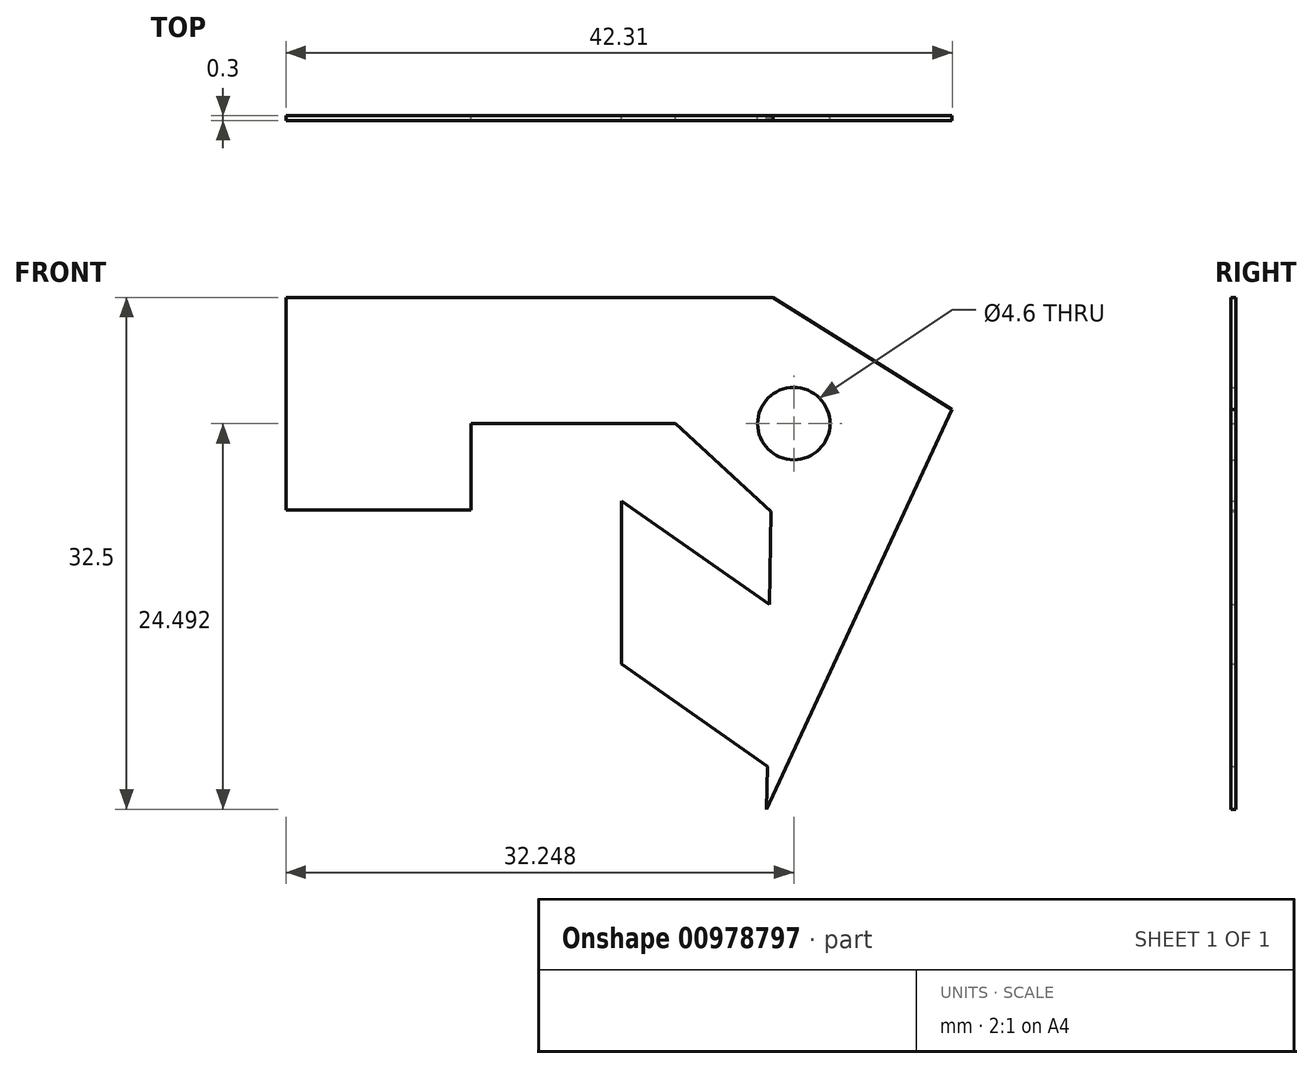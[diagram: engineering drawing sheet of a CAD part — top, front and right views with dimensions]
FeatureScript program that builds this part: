
annotation { "Feature Type Name" : "Feature", "Feature Type Description" : "" }
export const myFeature = defineFeature(function(context is Context, id is Id, definition is map)
    precondition{}
    {
        {
            var Q0;
            Q0=qCreatedBy(makeId("Front.planeOp"),FACE);
            var sketch = newSketch(context, id + "F0", { "sketchPlane" : qUnion([Q0])});
            skLineSegment(sketch, "E0", {"start": v(-25.77, 44.55) * mm, "end": v(5.15, 44.55) * mm});
            skLineSegment(sketch, "E1", {"start": v(5.15, 44.55) * mm, "end": v(16.54, 37.45) * mm});
            skLineSegment(sketch, "E2", {"start": v(16.54, 37.45) * mm, "end": v(4.75, 12.05) * mm});
            skLineSegment(sketch, "E3", {"start": v(16.54, 37.45) * mm, "end": v(16.54, 12.05) * mm, "construction": true});
            skLineSegment(sketch, "E4", {"start": v(4.75, 12.05) * mm, "end": v(16.54, 12.05) * mm, "construction": true});
            skLineSegment(sketch, "E5", {"start": v(-25.77, 44.55) * mm, "end": v(-25.77, 31.05) * mm});
            skLineSegment(sketch, "E6", {"start": v(-25.77, 31.05) * mm, "end": v(-14.03, 31.05) * mm});
            skLineSegment(sketch, "E7", {"start": v(-14.03, 31.05) * mm, "end": v(-14.03, 36.56) * mm});
            skLineSegment(sketch, "E8", {"start": v(-14.03, 36.56) * mm, "end": v(-1.03, 36.56) * mm});
            skLineSegment(sketch, "E9", {"start": v(-1.03, 36.56) * mm, "end": v(5.03, 30.96) * mm});
            skLineSegment(sketch, "E10", {"start": v(5.03, 30.96) * mm, "end": v(4.75, 12.05) * mm, "construction": true});
            skCircle(sketch, "E11", {"center": v(6.48, 36.54) * mm, "radius": 2.3 * mm});
            skLineSegment(sketch, "E12", {"start": v(4.95, 25.04) * mm, "end": v(-4.48, 31.63) * mm});
            skLineSegment(sketch, "E13", {"start": v(-4.48, 31.63) * mm, "end": v(-4.48, 21.26) * mm});
            skLineSegment(sketch, "E14", {"start": v(-4.48, 21.26) * mm, "end": v(4.8, 14.78) * mm});
            skLineSegment(sketch, "E15", {"start": v(5.03, 30.96) * mm, "end": v(4.95, 25.04) * mm});
            skLineSegment(sketch, "E16", {"start": v(4.8, 14.78) * mm, "end": v(4.75, 12.05) * mm});
            skSolve(sketch);
        }
        {
            var Q0;
            Q0=makeQuery(id+"F0.imprint","IMPRINT",FACE,{"disambiguationData":[TD([[makeQuery(id+"F0.imprint","IMPRINT",EDGE,{"derivedFrom":sQuery(id+"F0.wireOp",EDGE,"E0")}),-1.0]])]});
            extrude(context, id + "F1", {"entities" : qUnion([Q0]), "depth" : 0.3 * mm, "offsetDistance" : 25 * mm});
        }
    });
